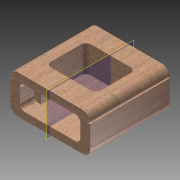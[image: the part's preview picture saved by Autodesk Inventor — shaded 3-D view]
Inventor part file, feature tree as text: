
AUTODESK INVENTOR PART (.ipt)
format: ipt  version: 2015 (Build 190159000, 159)  size: 242,176 bytes
history: native  units: in
note: dims shown in document units (in); Inventor stores cm internally (conversion verified against a paired STEP export)
features: extrude x5, sketch x5, fillet x2
ambient origin geometry x8: Origin, YZ Plane, XZ Plane, XY Plane, X Axis, Y Axis, Z Axis, Center Point
bodies: Solid1 (feature_tree)
feature tree (12):
  extrude  "Extrusion1"  Depth=1.53in
  extrude  "Extrusion2"  Depth=2.4in
  extrude  "Extrusion3"  Depth=0.57in TaperAngle=0.0deg
  extrude  "Extrusion4"  Depth=2.5in
  fillet  "Fillet1"  Radius=1.0in
  fillet  "Fillet2"  Radius=0.57in
  extrude  "Extrusion5"  Depth=0.82in
  sketch  "Sketch1"  dims[d0=3.17in d1=1.53in]
  sketch  "Sketch2"  dims[d2=3.17in d3=0.0in d4=2.4in]
  sketch  "Sketch3"  dims[d5=0.93in d7=0.57in d8=0.0in]
  sketch  "Sketch4"  dims[d9=0.2in d10=2.5in d11=1.0in d12=0.57in d13=0.0in]
  sketch  "Sketch6"  dims[d14=0.3in d15=0.82in d16=1.59in d17=1.975in d18=1.07in d19=0.0in d20=0.06in d21=0.3in d23=0.01in d26=0.65in d28=0.65in d30=0.0in d31=0.0in d32=1.0in d33=0.0in]
